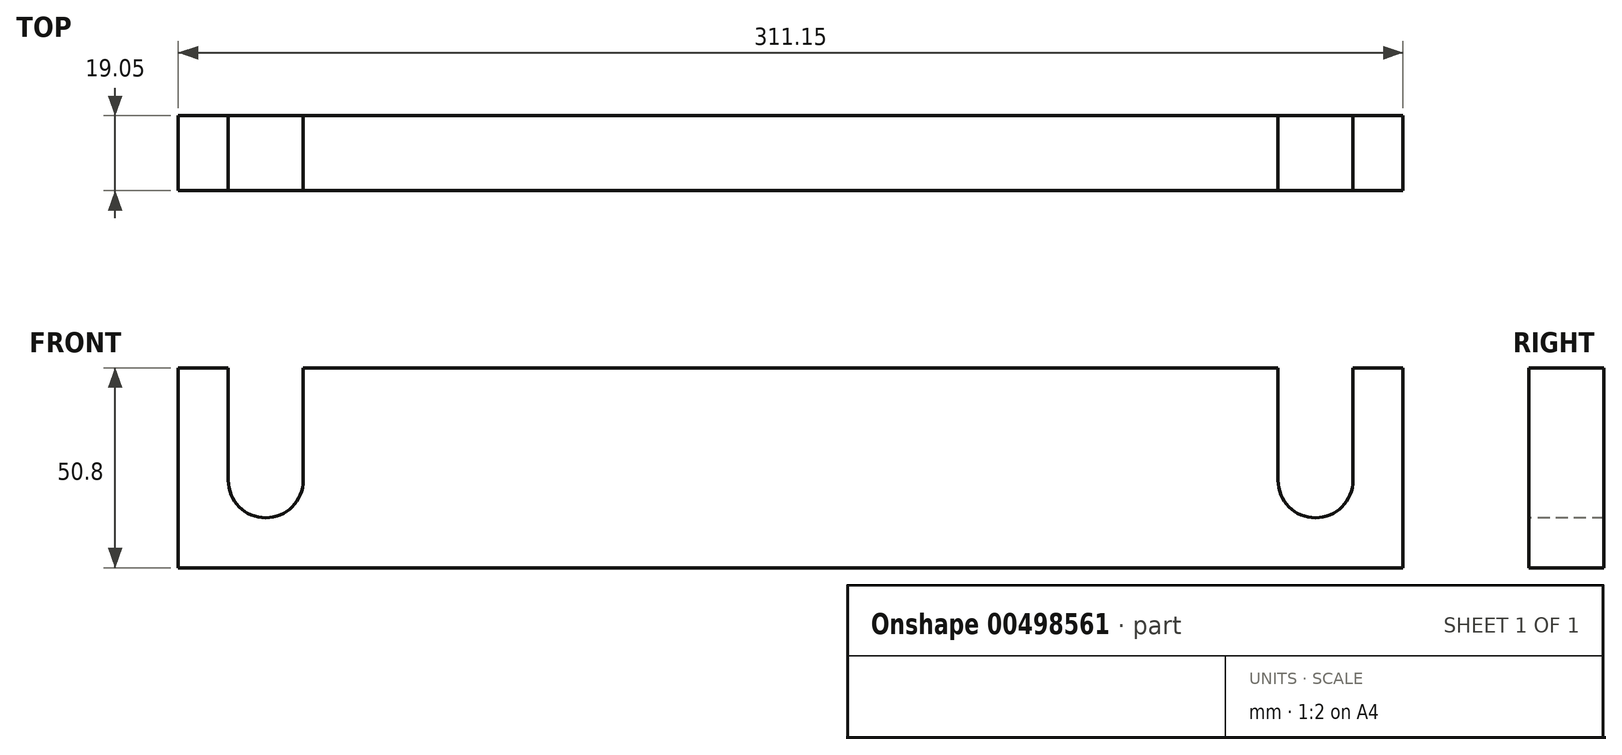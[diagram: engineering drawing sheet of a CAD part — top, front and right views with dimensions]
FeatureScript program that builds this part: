
annotation { "Feature Type Name" : "Feature", "Feature Type Description" : "" }
export const myFeature = defineFeature(function(context is Context, id is Id, definition is map)
    precondition{}
    {
        {
            var Q0;
            Q0=qCreatedBy(makeId("Front.planeOp"),FACE);
            var sketch = newSketch(context, id + "F0", { "sketchPlane" : qUnion([Q0])});
            skLineSegment(sketch, "E0.bottom", {"start": v(0, 0) * mm, "end": v(311.15, 0) * mm});
            skLineSegment(sketch, "E0.top", {"start": v(0, 50.8) * mm, "end": v(311.15, 50.8) * mm});
            skLineSegment(sketch, "E0.left", {"start": v(0, 0) * mm, "end": v(0, 50.8) * mm});
            skLineSegment(sketch, "E0.right", {"start": v(311.15, 0) * mm, "end": v(311.15, 50.8) * mm});
            skSolve(sketch);
        }
        {
            var Q0;
            Q0 = qSketchRegion(id + "F0", true);
            extrude(context, id + "F1", {"entities" : qUnion([Q0]), "depth" : 19.05 * mm, "offsetDistance" : 25.4 * mm});
        }
        {
            var Q0;
            Q0=makeQuery(id+"F1.opExtrude","CAP_FACE",FACE,{"disambiguationData":[OSD([sQuery(id+"F0.wireOp",EDGE,"E0.bottom"),sQuery(id+"F0.wireOp",EDGE,"E0.top"),sQuery(id+"F0.wireOp",EDGE,"E0.left"),sQuery(id+"F0.wireOp",EDGE,"E0.right")])],"isStart":false});
            var sketch = newSketch(context, id + "F2", { "sketchPlane" : qUnion([Q0])});
            skLineSegment(sketch, "E1.bottom", {"start": v(12.7, 50.8) * mm, "end": v(31.75, 50.8) * mm});
            skLineSegment(sketch, "E1.top", {"start": v(22.23, 12.7) * mm, "end": v(22.23, 12.7) * mm});
            skLineSegment(sketch, "E1.left", {"start": v(12.7, 50.8) * mm, "end": v(12.7, 22.23) * mm});
            skLineSegment(sketch, "E1.right", {"start": v(31.75, 50.8) * mm, "end": v(31.75, 22.23) * mm});
            skLineSegment(sketch, "E2.bottom", {"start": v(279.4, 50.8) * mm, "end": v(298.45, 50.8) * mm});
            skLineSegment(sketch, "E2.top", {"start": v(288.93, 12.7) * mm, "end": v(288.93, 12.7) * mm});
            skLineSegment(sketch, "E2.left", {"start": v(279.4, 50.8) * mm, "end": v(279.4, 22.23) * mm});
            skLineSegment(sketch, "E2.right", {"start": v(298.45, 50.8) * mm, "end": v(298.45, 22.23) * mm});
            skPoint(sketch, "E3.visualSharp", {"position": v(12.7, 12.7) * mm});
            skArc(sketch, "E3.filletArc", {"start": v(12.7, 22.23) * mm, "mid": v(15.49, 15.49) * mm, "end": v(22.23, 12.7) * mm});
            skPoint(sketch, "E4.visualSharp", {"position": v(31.75, 12.7) * mm});
            skArc(sketch, "E4.filletArc", {"start": v(22.23, 12.7) * mm, "mid": v(28.96, 15.49) * mm, "end": v(31.75, 22.23) * mm});
            skPoint(sketch, "E5.visualSharp", {"position": v(279.4, 12.7) * mm});
            skArc(sketch, "E5.filletArc", {"start": v(279.4, 22.23) * mm, "mid": v(282.19, 15.49) * mm, "end": v(288.93, 12.7) * mm});
            skPoint(sketch, "E6.visualSharp", {"position": v(298.45, 12.7) * mm});
            skArc(sketch, "E6.filletArc", {"start": v(288.93, 12.7) * mm, "mid": v(295.66, 15.49) * mm, "end": v(298.45, 22.23) * mm});
            skSolve(sketch);
        }
        {
            var Q0;
            Q0 = qSketchRegion(id + "F2", true);
            extrude(context, id + "F3", {"entities" : qUnion([Q0]), "operationType" : NewBodyOperationType.REMOVE, "endBound" : BoundingType.THROUGH_ALL, "oppositeDirection" : true, "depth" : 25.4 * mm, "offsetDistance" : 25.4 * mm});
        }
    });
